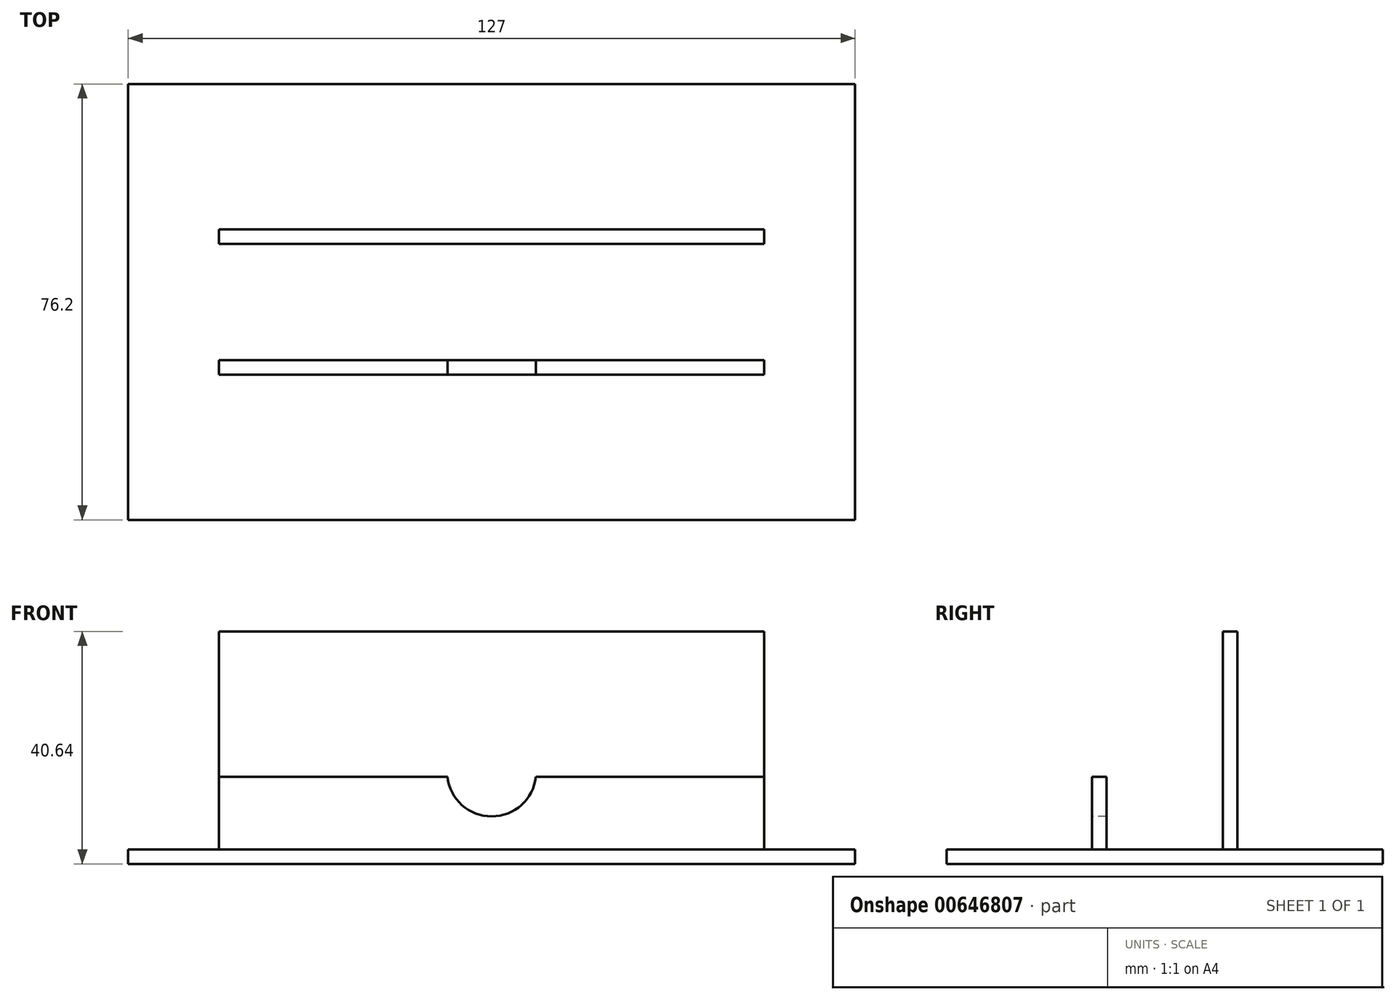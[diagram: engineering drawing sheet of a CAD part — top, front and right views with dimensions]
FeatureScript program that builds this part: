
annotation { "Feature Type Name" : "Feature", "Feature Type Description" : "" }
export const myFeature = defineFeature(function(context is Context, id is Id, definition is map)
    precondition{}
    {
        {
            var Q0;
            Q0=qCreatedBy(makeId("Top.planeOp"),FACE);
            var sketch = newSketch(context, id + "F0", { "sketchPlane" : qUnion([Q0])});
            skLineSegment(sketch, "E0.bottom", {"start": v(47.63, -12.7) * mm, "end": v(-47.63, -12.7) * mm});
            skLineSegment(sketch, "E0.top", {"start": v(47.63, 12.7) * mm, "end": v(-47.63, 12.7) * mm});
            skLineSegment(sketch, "E0.left", {"start": v(47.63, -12.7) * mm, "end": v(47.63, 12.7) * mm});
            skLineSegment(sketch, "E0.right", {"start": v(-47.63, -12.7) * mm, "end": v(-47.63, 12.7) * mm});
            skPoint(sketch, "E0.middle", {"position": v(0, 0) * mm});
            skSolve(sketch);
        }
        {
            var Q0;
            Q0=makeQuery(id+"F0.imprint","IMPRINT",FACE,{"disambiguationData":[TD([[makeQuery(id+"F0.imprint","IMPRINT",EDGE,{"derivedFrom":sQuery(id+"F0.wireOp",EDGE,"E0.bottom")}),-1.0]])]});
            extrude(context, id + "F1", {"entities" : qUnion([Q0]), "depth" : 12.7 * mm, "offsetDistance" : 25.4 * mm});
        }
        {
            var Q0;
            Q0=qCreatedBy(makeId("Top.planeOp"),FACE);
            var sketch = newSketch(context, id + "F2", { "sketchPlane" : qUnion([Q0])});
            skLineSegment(sketch, "E1.bottom", {"start": v(63.5, 38.1) * mm, "end": v(-63.5, 38.1) * mm});
            skLineSegment(sketch, "E1.top", {"start": v(63.5, -38.1) * mm, "end": v(-63.5, -38.1) * mm});
            skLineSegment(sketch, "E1.left", {"start": v(63.5, 38.1) * mm, "end": v(63.5, -38.1) * mm});
            skLineSegment(sketch, "E1.right", {"start": v(-63.5, 38.1) * mm, "end": v(-63.5, -38.1) * mm});
            skPoint(sketch, "E1.middle", {"position": v(0, 0) * mm});
            skSolve(sketch);
        }
        {
            var Q0;
            Q0=makeQuery(id+"F2.imprint","IMPRINT",FACE,{"disambiguationData":[TD([[makeQuery(id+"F2.imprint","IMPRINT",EDGE,{"derivedFrom":sQuery(id+"F2.wireOp",EDGE,"E1.bottom")}),1.0]])]});
            extrude(context, id + "F3", {"entities" : qUnion([Q0]), "operationType" : NewBodyOperationType.ADD, "oppositeDirection" : true, "depth" : 2.54 * mm, "offsetDistance" : 25.4 * mm});
        }
        {
            var Q0;
            Q0=makeQuery(id+"F1.opExtrude","CAP_FACE",FACE,{"disambiguationData":[OSD([sQuery(id+"F0.wireOp",EDGE,"E0.bottom"),sQuery(id+"F0.wireOp",EDGE,"E0.top"),sQuery(id+"F0.wireOp",EDGE,"E0.left"),sQuery(id+"F0.wireOp",EDGE,"E0.right")])],"isStart":false});
            shell(context, id + "F4", {"entities" : qUnion([Q0]), "thickness" : 2.54 * mm});
        }
        {
            var Q0;
            Q0=makeQuery(id+"F4.opShell","OFFSET_FACE",FACE,{"disambiguationData":[OSD([sQuery(id+"F0.wireOp",EDGE,"E0.right")])]});
            extrude(context, id + "F5", {"entities" : qUnion([Q0]), "operationType" : NewBodyOperationType.REMOVE, "oppositeDirection" : true, "depth" : 25.4 * mm, "offsetDistance" : 25.4 * mm});
        }
        {
            var Q0;
            Q0=makeQuery(id+"F4.opShell","OFFSET_FACE",FACE,{"disambiguationData":[OSD([sQuery(id+"F0.wireOp",EDGE,"E0.left")])]});
            extrude(context, id + "F6", {"entities" : qUnion([Q0]), "operationType" : NewBodyOperationType.REMOVE, "oppositeDirection" : true, "depth" : 25.4 * mm, "offsetDistance" : 25.4 * mm});
        }
        {
            var Q0;
            {var subQ0=sQuery(id+"F0.wireOp",EDGE,"E0.top");var subQ1=sQuery(id+"F0.wireOp",EDGE,"E0.right");var subQ2=sQuery(id+"F0.wireOp",EDGE,"E0.left");Q0=makeQuery(id+"F6.boolean.opBoolean","SPLIT",FACE,{"disambiguationData":[TD([makeQuery(id+"F1.opExtrude","SWEPT_FACE",FACE,{"disambiguationData":[OSD([subQ0])]})])],"derivedFrom":makeQuery(id+"F1.opExtrude","CAP_FACE",FACE,{"disambiguationData":[OSD([sQuery(id+"F0.wireOp",EDGE,"E0.bottom"),subQ0,subQ2,subQ1])],"isStart":false})});}
            extrude(context, id + "F7", {"entities" : qUnion([Q0]), "operationType" : NewBodyOperationType.ADD, "depth" : 25.4 * mm, "offsetDistance" : 25.4 * mm});
        }
        {
            var Q0;
            Q0=makeQuery(id+"F1.opExtrude","SWEPT_FACE",FACE,{"disambiguationData":[OSD([sQuery(id+"F0.wireOp",EDGE,"E0.bottom")])]});
            var sketch = newSketch(context, id + "F8", { "sketchPlane" : qUnion([Q0])});
            skSolve(sketch);
        }
        {
            var Q0;
            {var subQ0=sQuery(id+"F0.wireOp",EDGE,"E0.bottom");Q0=makeQuery(id+"F8.imprint","IMPRINT",FACE,{"disambiguationData":[TD([[makeQuery(id+"F8.imprint","IMPRINT",EDGE,{"derivedFrom":makeQuery(id+"F1.opExtrude","CAP_EDGE",EDGE,{"disambiguationData":[OSD([subQ0])],"isStart":false})}),1.0]])]});}
            var sketch = newSketch(context, id + "F9", { "sketchPlane" : qUnion([Q0])});
            skCircle(sketch, "E2", {"center": v(0, 13.52) * mm, "radius": 7.77 * mm});
            skSolve(sketch);
        }
        {
            var Q0;
            {var subQ0=sQuery(id+"F9.wireOp",EDGE,"E2");var subQ1=makeQuery(id+"F8.imprint","IMPRINT",EDGE,{"derivedFrom":makeQuery(id+"F1.opExtrude","CAP_EDGE",EDGE,{"disambiguationData":[OSD([sQuery(id+"F0.wireOp",EDGE,"E0.bottom")])],"isStart":false})});var subQ2=makeQuery(id+"F9.imprint","INTERSECT",VERTEX,{"disambiguationData":[OD(0.0)],"derivedFrom":[subQ1,subQ0]});Q0=makeQuery(id+"F9.imprint","IMPRINT",FACE,{"disambiguationData":[TD([[makeQuery(id+"F9.imprint","IMPRINT",EDGE,{"disambiguationData":[TD([[subQ2,-1.0]])],"derivedFrom":subQ0}),1.0]])]});}
            var Q1;
            {var subQ0=sQuery(id+"F9.wireOp",EDGE,"E2");var subQ1=makeQuery(id+"F8.imprint","IMPRINT",EDGE,{"derivedFrom":makeQuery(id+"F1.opExtrude","CAP_EDGE",EDGE,{"disambiguationData":[OSD([sQuery(id+"F0.wireOp",EDGE,"E0.bottom")])],"isStart":false})});var subQ2=makeQuery(id+"F9.imprint","INTERSECT",VERTEX,{"disambiguationData":[OD(0.0)],"derivedFrom":[subQ1,subQ0]});Q1=makeQuery(id+"F9.imprint","IMPRINT",FACE,{"disambiguationData":[TD([[makeQuery(id+"F9.imprint","IMPRINT",EDGE,{"disambiguationData":[TD([[subQ2,1.0]])],"derivedFrom":subQ0}),1.0]])]});}
            extrude(context, id + "F10", {"entities" : qUnion([Q0, Q1]), "operationType" : NewBodyOperationType.REMOVE, "oppositeDirection" : true, "depth" : 5.08 * mm, "offsetDistance" : 25.4 * mm});
        }
    });
